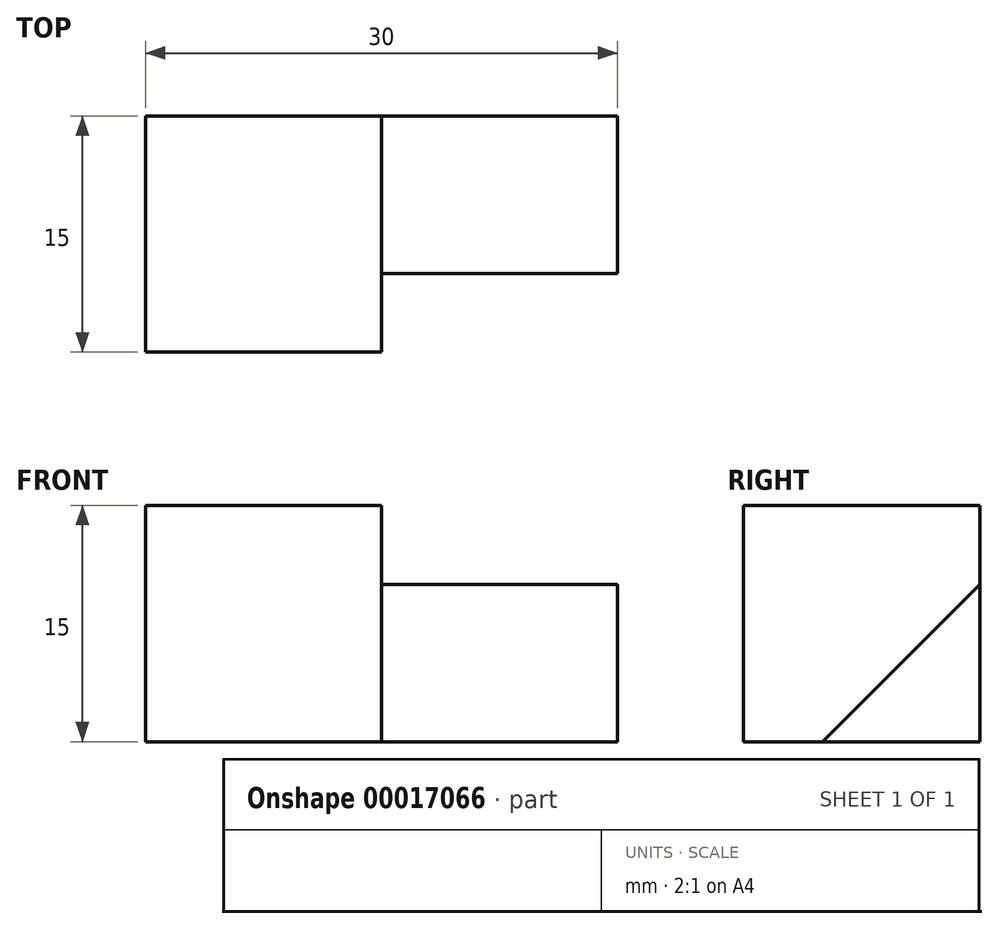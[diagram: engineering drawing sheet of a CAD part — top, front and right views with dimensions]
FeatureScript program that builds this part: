
annotation { "Feature Type Name" : "Feature", "Feature Type Description" : "" }
export const myFeature = defineFeature(function(context is Context, id is Id, definition is map)
    precondition{}
    {
        {
            var Q0;
            Q0=qCreatedBy(makeId("Right.planeOp"),FACE);
            var sketch = newSketch(context, id + "F0", { "sketchPlane" : qUnion([Q0])});
            skLineSegment(sketch, "E0", {"start": v(23.56, 25.76) * mm, "end": v(13.56, 15.76) * mm});
            skLineSegment(sketch, "E1", {"start": v(13.56, 15.76) * mm, "end": v(23.56, 15.76) * mm});
            skLineSegment(sketch, "E2", {"start": v(23.56, 25.76) * mm, "end": v(23.56, 15.76) * mm});
            skLineSegment(sketch, "E3.bottom", {"start": v(23.56, 15.76) * mm, "end": v(8.56, 15.76) * mm});
            skLineSegment(sketch, "E3.top", {"start": v(23.56, 30.76) * mm, "end": v(8.56, 30.76) * mm});
            skLineSegment(sketch, "E3.left", {"start": v(23.56, 15.76) * mm, "end": v(23.56, 30.76) * mm});
            skLineSegment(sketch, "E3.right", {"start": v(8.56, 15.76) * mm, "end": v(8.56, 30.76) * mm});
            skSolve(sketch);
        }
        {
            var Q0;
            {var subQ3=sQuery(id+"F0.wireOp",EDGE,"E0");Q0=makeQuery(id+"F0.imprint","IMPRINT",FACE,{"disambiguationData":[TD([[makeQuery(id+"F0.imprint","IMPRINT",EDGE,{"derivedFrom":subQ3}),-1.0]])]});}
            var Q1;
            {var subQ3=sQuery(id+"F0.wireOp",EDGE,"E0");Q1=makeQuery(id+"F0.imprint","IMPRINT",FACE,{"disambiguationData":[TD([[makeQuery(id+"F0.imprint","IMPRINT",EDGE,{"derivedFrom":subQ3}),1.0]])]});}
            extrude(context, id + "F1", {"entities" : qUnion([Q0, Q1]), "oppositeDirection" : true, "depth" : 15 * mm});
        }
        {
            var Q0;
            Q0=makeQuery(id+"F1.opExtrude","CAP_FACE",FACE,{"disambiguationData":[OSD([sQuery(id+"F0.wireOp",EDGE,"E3.bottom"),sQuery(id+"F0.wireOp",EDGE,"E3.top"),sQuery(id+"F0.wireOp",EDGE,"E3.left"),sQuery(id+"F0.wireOp",EDGE,"E3.right")])],"isStart":true});
            var sketch = newSketch(context, id + "F2", { "sketchPlane" : qUnion([Q0])});
            skLineSegment(sketch, "E4", {"start": v(23.56, 15.76) * mm, "end": v(13.56, 15.76) * mm});
            skLineSegment(sketch, "E5", {"start": v(23.56, 15.76) * mm, "end": v(23.56, 25.76) * mm});
            skLineSegment(sketch, "E6", {"start": v(23.56, 25.76) * mm, "end": v(13.56, 15.76) * mm});
            skSolve(sketch);
        }
        {
            var Q0;
            Q0 = qSketchRegion(id + "F2", true);
            extrude(context, id + "F3", {"entities" : qUnion([Q0]), "operationType" : NewBodyOperationType.ADD, "depth" : 15 * mm});
        }
        {
            var Q0;
            Q0 = qSketchRegion(id + "F2", true);
            extrude(context, id + "F4", {"entities" : qUnion([Q0]), "operationType" : NewBodyOperationType.ADD, "depth" : 15 * mm});
        }
    });
